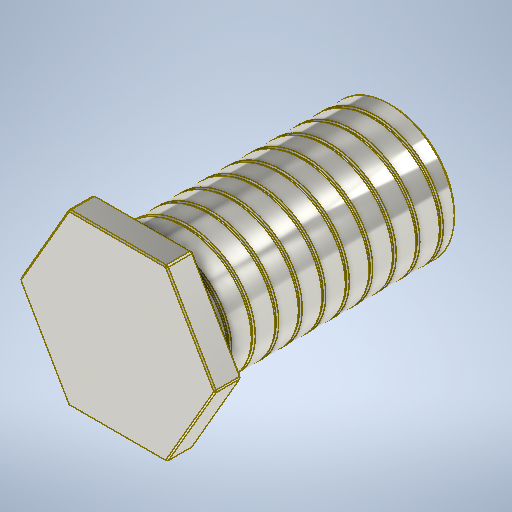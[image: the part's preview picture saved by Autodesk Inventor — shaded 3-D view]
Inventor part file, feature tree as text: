
AUTODESK INVENTOR PART (.ipt)
format: ipt  version: 2025.2 (Build 292293000, 293)  size: 644,096 bytes
history: native  units: mm
features: sketch x5, extrude x3, chamfer x2, helix x1
ambient origin geometry x8: Origin, YZ Plane, XZ Plane, XY Plane, X Axis, Y Axis, Z Axis, Center Point
bodies: Solid1 (feature_tree)
feature tree (11):
  extrude  "Extrusion1"  Depth=200.0mm TaperAngle=0.0deg
  helix  "Coil1"  [1 undecoded]
  sketch  "Sketch3"  dims[d16=150.0mm d17=20.0mm d18=0.0mm]
  chamfer  "Chamfer1"  Distance=2.0mm Angle=45.0deg
  extrude  "Extrusion2"  Depth=20.0mm TaperAngle=0.0deg
  extrude  "Extrusion3"  Depth=1.0mm TaperAngle=45.0deg
  chamfer  "Chamfer2"  [1 undecoded]
  sketch  "Sketch1"  dims[d0=100.0mm d1=200.0mm d2=0.0mm d4=3.0mm]
  sketch  "Sketch2"  dims[d5=18.0mm d6=10.0mm d7=110.0mm d8=0.0mm d9=90.0deg d10=90.0deg d11=0.0mm d12=0.0mm d13=2.0mm d14=2.0mm d15=45.0deg]
  sketch  "Sketch4"  dims[d19=250.841mm d20=0.0mm d21=1.0mm d22=2.0mm d23=45.0deg]
  sketch  "Sketch5"
note: 2 required parameter values undecoded (feature->parameter linkage not recoverable at this tier; creation-order binding heuristic only, values carry confidence <= 0.55)
